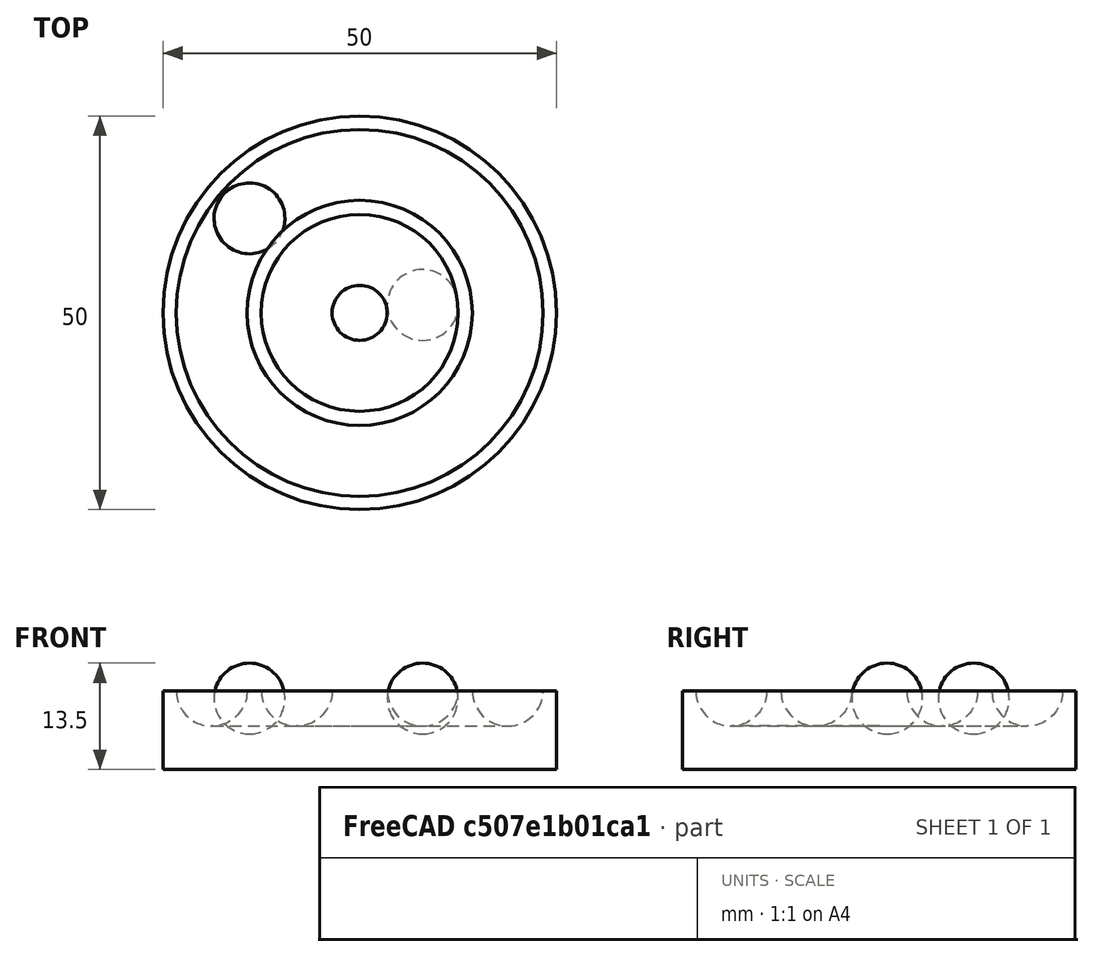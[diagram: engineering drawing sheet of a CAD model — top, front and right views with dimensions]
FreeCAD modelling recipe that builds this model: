
FCSTD DOCUMENT  (FreeCAD 0.21R33694 (Git))
Label: OJT1_T15R02_porta-bales
License: All rights reserved
LicenseURL: https://en.wikipedia.org/wiki/All_rights_reserved
objects: Part::Torus×2, Part::Cut×2, Part::Sphere×2, Part::Cylinder×1
note: 7 computed .brp shape members not serialized (recipe doc carries the construction recipe); baked Part::Feature solids carry a one-line shape summary decoded from their .brp

FEATURE [Part::Cylinder] Cylinder  label="Base"
  Angle = 360
  AttacherType = Attacher::AttachEngine3D
  FirstAngle = 0
  Height = 10
  Radius = 25
  SecondAngle = 0
FEATURE [Part::Torus] Torus  label="volta_1"
  Angle1 = -180
  Angle2 = 180
  Angle3 = 360
  AttacherType = Attacher::AttachEngine3D
  Placement = pos=(0,0,10) rot=(0,0,1;0rad)
  Radius1 = 8
  Radius2 = 4.5
FEATURE [Part::Torus] Torus001  label="volta_002"
  Angle1 = -180
  Angle2 = 180
  Angle3 = 360
  AttacherType = Attacher::AttachEngine3D
  Placement = pos=(0,0,10) rot=(0,0,1;0rad)
  Radius1 = 18.8
  Radius2 = 4.5
FEATURE [Part::Cut] Cut
  Base = -> Cylinder
  Tool = -> Torus
FEATURE [Part::Cut] Cut001  label="Guarda_caniques"
  Base = -> Cut
  Tool = -> Torus001
FEATURE [Part::Sphere] Sphere  label="Canica_1"
  Angle1 = -90
  Angle2 = 90
  Angle3 = 360
  AttacherType = Attacher::AttachEngine3D
  Placement = pos=(8,1,9) rot=(0,0,1;0rad)
  Radius = 4.5
FEATURE [Part::Sphere] Sphere001  label="Canica_2"
  Angle1 = -90
  Angle2 = 90
  Angle3 = 360
  AttacherType = Attacher::AttachEngine3D
  Placement = pos=(-14,12,9) rot=(0,0,1;0rad)
  Radius = 4.5
